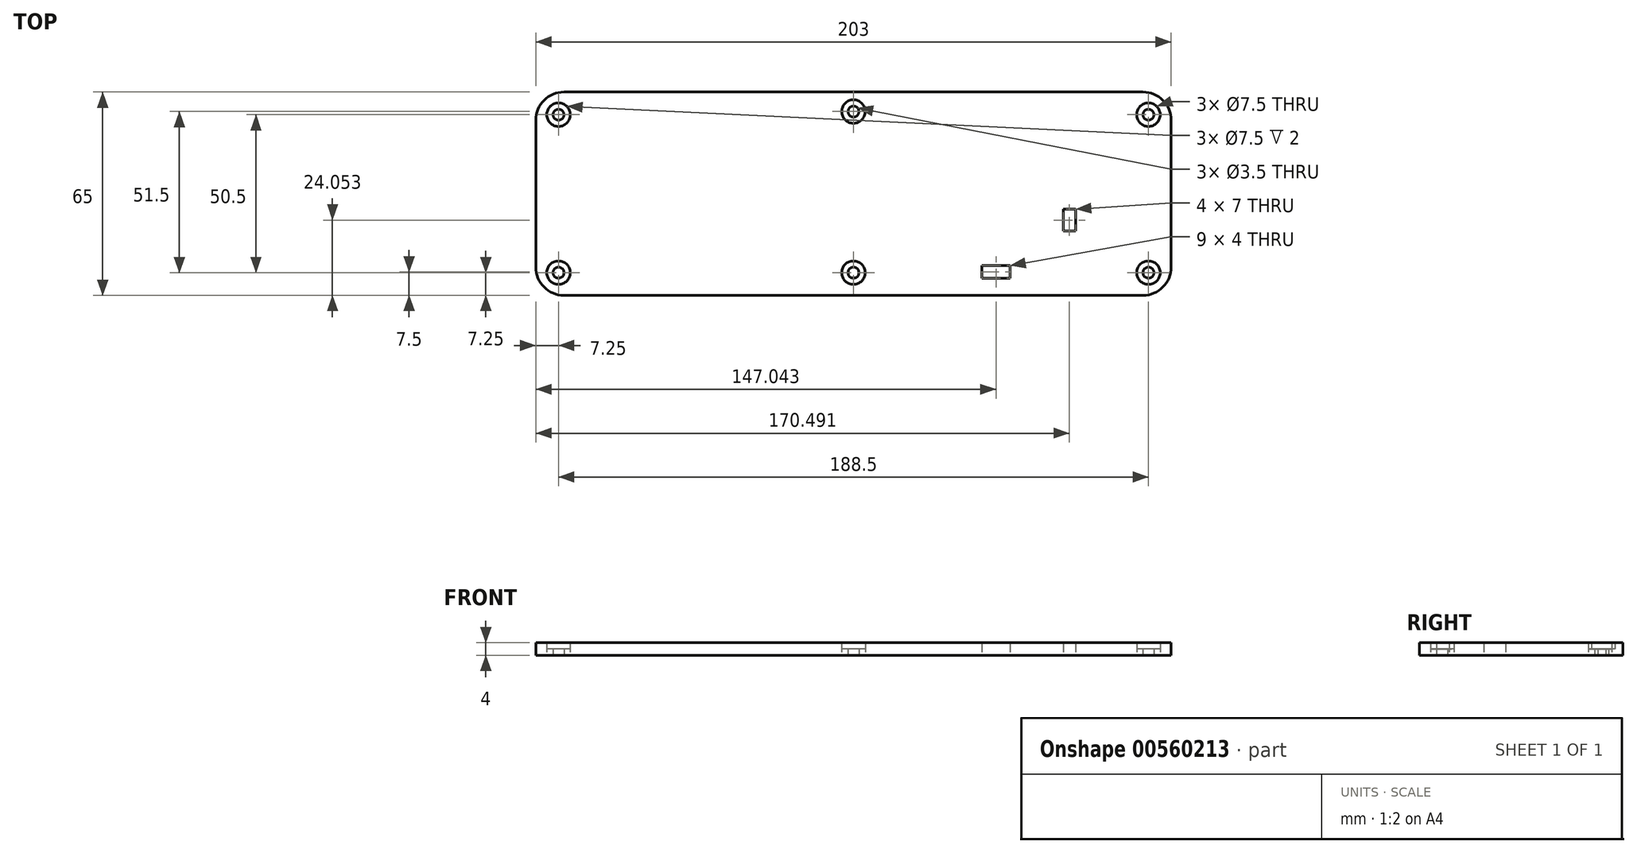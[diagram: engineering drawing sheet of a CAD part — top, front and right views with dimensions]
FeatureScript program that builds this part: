
annotation { "Feature Type Name" : "Feature", "Feature Type Description" : "" }
export const myFeature = defineFeature(function(context is Context, id is Id, definition is map)
    precondition{}
    {
        {
            var Q0;
            Q0=qCreatedBy(makeId("Top.planeOp"),FACE);
            var sketch = newSketch(context, id + "F0", { "sketchPlane" : qUnion([Q0])});
            skLineSegment(sketch, "E0.bottom", {"start": v(92.5, -32.5) * mm, "end": v(-92.5, -32.5) * mm});
            skLineSegment(sketch, "E0.top", {"start": v(92.5, 32.5) * mm, "end": v(-92.5, 32.5) * mm});
            skLineSegment(sketch, "E0.left", {"start": v(101.5, -23.5) * mm, "end": v(101.5, 23.5) * mm});
            skLineSegment(sketch, "E0.right", {"start": v(-101.5, -23.5) * mm, "end": v(-101.5, 23.5) * mm});
            skArc(sketch, "E1.filletArc", {"start": v(-92.5, 32.5) * mm, "mid": v(-98.86, 29.86) * mm, "end": v(-101.5, 23.5) * mm});
            skPoint(sketch, "E2.visualSharp", {"position": v(-101.5, -32.5) * mm});
            skArc(sketch, "E2.filletArc", {"start": v(-101.5, -23.5) * mm, "mid": v(-98.86, -29.86) * mm, "end": v(-92.5, -32.5) * mm});
            skPoint(sketch, "E3.visualSharp", {"position": v(101.5, -32.5) * mm});
            skArc(sketch, "E3.filletArc", {"start": v(92.5, -32.5) * mm, "mid": v(98.86, -29.86) * mm, "end": v(101.5, -23.5) * mm});
            skPoint(sketch, "E4.visualSharp", {"position": v(101.5, 32.5) * mm});
            skArc(sketch, "E4.filletArc", {"start": v(101.5, 23.5) * mm, "mid": v(98.86, 29.86) * mm, "end": v(92.5, 32.5) * mm});
            skCircle(sketch, "E5", {"center": v(-94.25, 25.25) * mm, "radius": 1.75 * mm});
            skCircle(sketch, "E6.MirrorC", {"center": v(-94.25, -25.25) * mm, "radius": 1.75 * mm});
            skCircle(sketch, "E7.MirrorC", {"center": v(94.25, -25.25) * mm, "radius": 1.75 * mm});
            skPoint(sketch, "E8.endSnap0", {"position": v(0, -32.5) * mm});
            skCircle(sketch, "E9", {"center": v(0, 26.25) * mm, "radius": 1.75 * mm});
            skCircle(sketch, "E10.MirrorC", {"center": v(0, -25.25) * mm, "radius": 1.75 * mm});
            skCircle(sketch, "E11", {"center": v(-94.25, -25.25) * mm, "radius": 3.75 * mm});
            skCircle(sketch, "E12", {"center": v(0, -25.25) * mm, "radius": 3.75 * mm});
            skCircle(sketch, "E13", {"center": v(-94.25, 25.25) * mm, "radius": 3.75 * mm});
            skCircle(sketch, "E14", {"center": v(0, 26.25) * mm, "radius": 3.75 * mm});
            skCircle(sketch, "E15", {"center": v(94.25, -25.25) * mm, "radius": 3.75 * mm});
            skCircle(sketch, "E16.MirrorC", {"center": v(94.25, 25.25) * mm, "radius": 1.75 * mm});
            skCircle(sketch, "E17.MirrorC", {"center": v(94.25, 25.25) * mm, "radius": 3.75 * mm});
            skLineSegment(sketch, "E18.bottom", {"start": v(67, -11.95) * mm, "end": v(71, -11.95) * mm});
            skLineSegment(sketch, "E18.top", {"start": v(67, -4.95) * mm, "end": v(71, -4.95) * mm});
            skLineSegment(sketch, "E18.left", {"start": v(67, -11.95) * mm, "end": v(67, -4.95) * mm});
            skLineSegment(sketch, "E18.right", {"start": v(71, -11.95) * mm, "end": v(71, -4.95) * mm});
            skLineSegment(sketch, "E19", {"start": v(0, 11.94) * mm, "end": v(0, -9.62) * mm, "construction": true});
            skLineSegment(sketch, "E20", {"start": v(-19.79, 0) * mm, "end": v(11.58, 0) * mm, "construction": true});
            skLineSegment(sketch, "E21.MirrorCS", {"start": v(41.04, -27) * mm, "end": v(41.04, -23) * mm});
            skLineSegment(sketch, "E22.MirrorCS", {"start": v(41.04, -27) * mm, "end": v(50.04, -27) * mm});
            skLineSegment(sketch, "E23.MirrorCS", {"start": v(41.04, -23) * mm, "end": v(50.04, -23) * mm});
            skLineSegment(sketch, "E24.MirrorCS", {"start": v(50.04, -27) * mm, "end": v(50.04, -23) * mm});
            skLineSegment(sketch, "E25", {"start": v(0, 32.5) * mm, "end": v(0, 26.25) * mm, "construction": true});
            skSolve(sketch);
        }
        {
            var Q0;
            Q0=qSketchRegion(id+"F0",true);
            extrude(context, id + "F1", {"entities" : qUnion([Q0]), "depth" : 4 * mm, "offsetDistance" : 25 * mm});
        }
        {
            var Q0;
            Q0=makeQuery(id+"F0.imprint","IMPRINT",FACE,{"disambiguationData":[TD([[makeQuery(id+"F0.imprint","IMPRINT",EDGE,{"derivedFrom":sQuery(id+"F0.wireOp",EDGE,"E7.MirrorC")}),-1.0]])]});
            var Q1;
            Q1=makeQuery(id+"F0.imprint","IMPRINT",FACE,{"disambiguationData":[TD([[makeQuery(id+"F0.imprint","IMPRINT",EDGE,{"derivedFrom":sQuery(id+"F0.wireOp",EDGE,"E10.MirrorC")}),1.0]])]});
            var Q2;
            Q2=makeQuery(id+"F0.imprint","IMPRINT",FACE,{"disambiguationData":[TD([[makeQuery(id+"F0.imprint","IMPRINT",EDGE,{"derivedFrom":sQuery(id+"F0.wireOp",EDGE,"E9")}),-1.0]])]});
            var Q3;
            Q3=makeQuery(id+"F0.imprint","IMPRINT",FACE,{"disambiguationData":[TD([[makeQuery(id+"F0.imprint","IMPRINT",EDGE,{"derivedFrom":sQuery(id+"F0.wireOp",EDGE,"E16.MirrorC")}),1.0]])]});
            var Q4;
            Q4=makeQuery(id+"F0.imprint","IMPRINT",FACE,{"disambiguationData":[TD([[makeQuery(id+"F0.imprint","IMPRINT",EDGE,{"derivedFrom":sQuery(id+"F0.wireOp",EDGE,"E6.MirrorC")}),1.0]])]});
            var Q5;
            Q5=makeQuery(id+"F0.imprint","IMPRINT",FACE,{"disambiguationData":[TD([[makeQuery(id+"F0.imprint","IMPRINT",EDGE,{"derivedFrom":sQuery(id+"F0.wireOp",EDGE,"E5")}),-1.0]])]});
            extrude(context, id + "F2", {"entities" : qUnion([Q0, Q1, Q2, Q3, Q4, Q5]), "operationType" : NewBodyOperationType.ADD, "depth" : 2 * mm, "offsetDistance" : 25 * mm});
        }
    });
